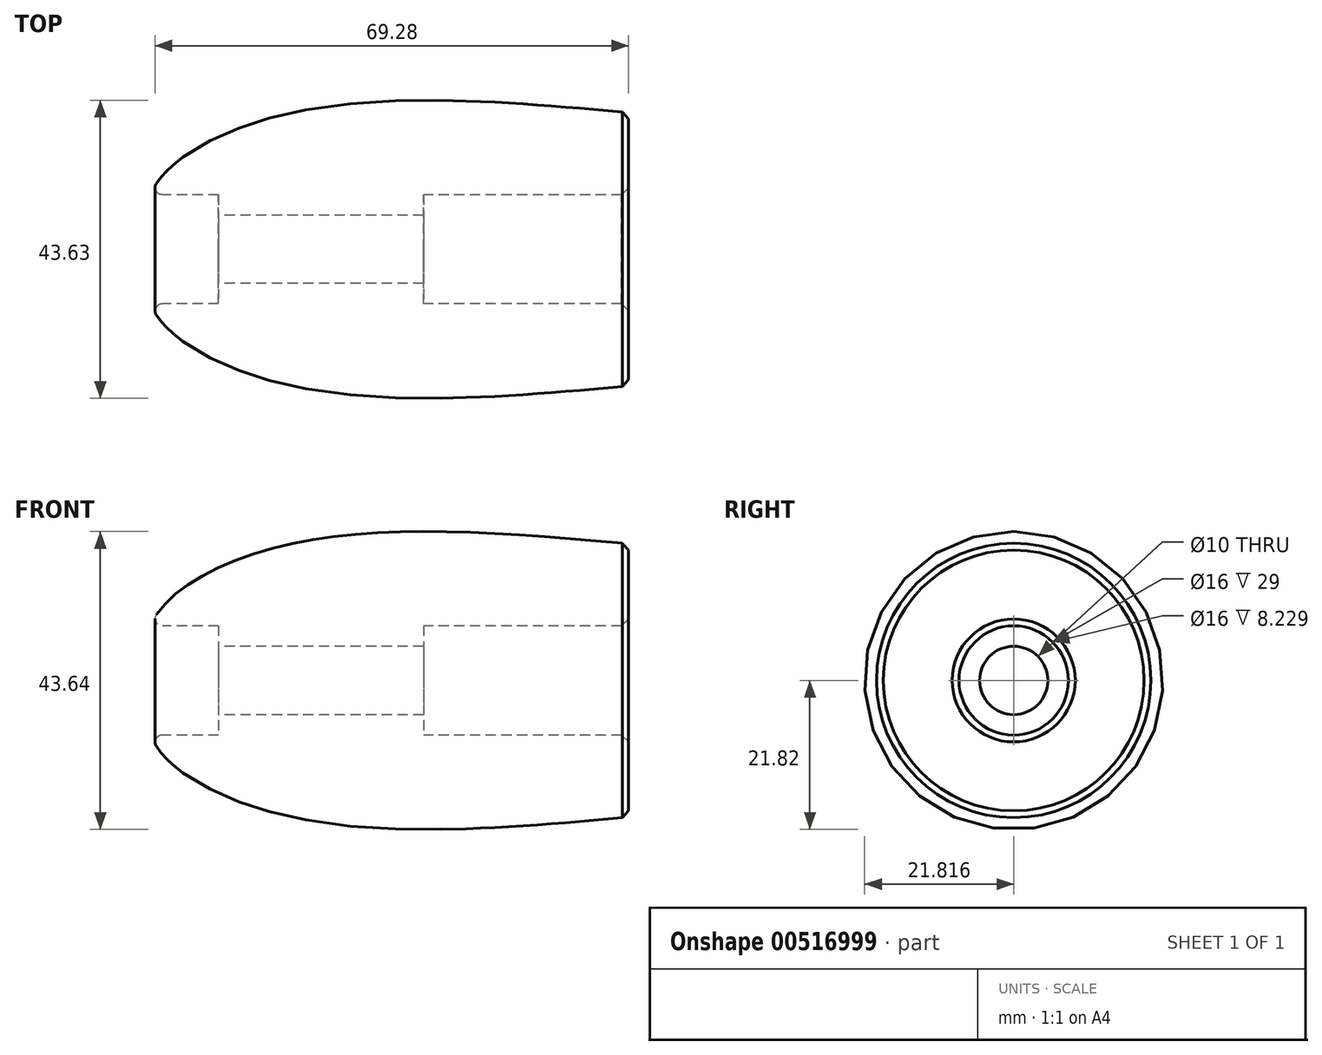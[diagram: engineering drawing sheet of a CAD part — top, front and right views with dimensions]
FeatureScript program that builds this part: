
annotation { "Feature Type Name" : "Feature", "Feature Type Description" : "" }
export const myFeature = defineFeature(function(context is Context, id is Id, definition is map)
    precondition{}
    {
        {
            var Q0;
            Q0=qCreatedBy(makeId("Top.planeOp"),FACE);
            var sketch = newSketch(context, id + "F0", { "sketchPlane" : qUnion([Q0])});
            skLineSegment(sketch, "E0", {"start": v(-21.26, 14.57) * mm, "end": v(8.74, 14.57) * mm});
            skLineSegment(sketch, "E1", {"start": v(8.74, 14.57) * mm, "end": v(8.74, 17.57) * mm});
            skLineSegment(sketch, "E2", {"start": v(8.74, 17.57) * mm, "end": v(38.74, 17.57) * mm});
            skLineSegment(sketch, "E3", {"start": v(38.74, 17.57) * mm, "end": v(38.74, 29.57) * mm});
            skLineSegment(sketch, "E4", {"start": v(-21.26, 14.57) * mm, "end": v(-21.26, 17.57) * mm});
            skLineSegment(sketch, "E5", {"start": v(-21.26, 17.57) * mm, "end": v(-29.5, 17.57) * mm});
            skFitSpline(sketch, "E6", {"points": [v(38.74, 29.57) * mm, v(-10.56, 29.57) * mm, v(-31.26, 17.57) * mm], "startDerivative": vector(-93.44, 8.61) * mm, "endDerivative": vector(-17.87, -40.83) * mm});
            skArc(sketch, "E7.filletArc", {"start": v(-30.36, 19.2) * mm, "mid": v(-30.42, 18.12) * mm, "end": v(-29.5, 17.57) * mm});
            skLineSegment(sketch, "E8", {"start": v(-31.2, 9.57) * mm, "end": v(38.91, 9.57) * mm});
            skSolve(sketch);
        }
        {
            var Q0;
            Q0=makeQuery(id+"F0.imprint","IMPRINT",FACE,{"disambiguationData":[TD([[makeQuery(id+"F0.imprint","IMPRINT",EDGE,{"derivedFrom":sQuery(id+"F0.wireOp",EDGE,"E0")}),1.0]])]});
            var Q1;
            Q1=sQuery(id+"F0.wireOp",EDGE,"E8");
            revolve(context, id + "F1", {"entities" : qUnion([Q0]), "axis" : qUnion([Q1]), "revolveType" : RevolveType.FULL});
        }
        {
            var Q0;
            Q0=makeQuery(id+"F1.opRevolve","SWEPT_EDGE",EDGE,{"disambiguationData":[OSD([sQuery(id+"F0.wireOp",EDGE,"E3"),sQuery(id+"F0.wireOp",EDGE,"E6")])]});
            var Q1;
            Q1=makeQuery(id+"F1.opRevolve","SWEPT_EDGE",EDGE,{"disambiguationData":[OSD([sQuery(id+"F0.wireOp",EDGE,"E2"),sQuery(id+"F0.wireOp",EDGE,"E3")])]});
            chamfer(context, id + "F2", {"entities" : qUnion([Q0, Q1]), "width" : 1 * mm, "tangentPropagation" : true});
        }
    });
